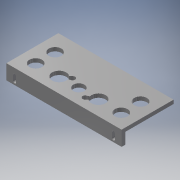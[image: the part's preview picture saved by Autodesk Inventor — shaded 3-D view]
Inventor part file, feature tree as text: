
AUTODESK INVENTOR PART (.ipt)
format: ipt  version: 2017 (Build 210142000, 142)  size: 238,592 bytes
history: native  units: mm (DEFAULTED — no unit token found)
features: extrude x6, sketch x6, projected_geometry x5
ambient origin geometry x8: Origin, YZ Plane, XZ Plane, XY Plane, X Axis, Y Axis, Z Axis, Center Point
bodies: Body1 (feature_tree)
feature tree (17):
  extrude  "Extrusion2"  Depth=70.0mm
  extrude  "Extrusion3"  Depth=20.0mm
  extrude  "Extrusion4"  Depth=15.0mm
  extrude  "Extrusion5"  Depth=7.0mm
  extrude  "Extrusion6"  Depth=7.0mm
  extrude  "Extrusion7"  Depth=15.0mm
  sketch  "Sketch1"  dims[d23=155.0mm d24=70.0mm]
  sketch  "Sketch2"  dims[d25=5.0mm d26=0.0mm d27=20.0mm]
  projected_geometry  "Projected Loop1"
  sketch  "Sketch3"  dims[d28=15.0mm d29=19.0mm]
  projected_geometry  "Projected Loop2"
  sketch  "Sketch4"  dims[d30=26.5mm d31=7.0mm]
  projected_geometry  "Projected Loop3"
  sketch  "Sketch5"  dims[d32=7.0mm d33=7.0mm]
  projected_geometry  "Projected Loop4"
  sketch  "Sketch6"  dims[d34=5.0mm d35=0.0mm d36=3.0mm d37=3.0mm d38=3.0mm d39=3.0mm d40=5.0mm d41=0.0mm d42=10.0mm d43=10.0mm d44=20.0mm d45=45.0mm d46=17.0mm d48=26.0mm d49=5.0mm d50=0.0mm d51=5.0mm d52=15.0mm d53=0.0mm d54=4.0mm d55=7.0mm d56=9.0mm d57=15.0mm d58=0.0mm]
  projected_geometry  "Projected Loop5"
